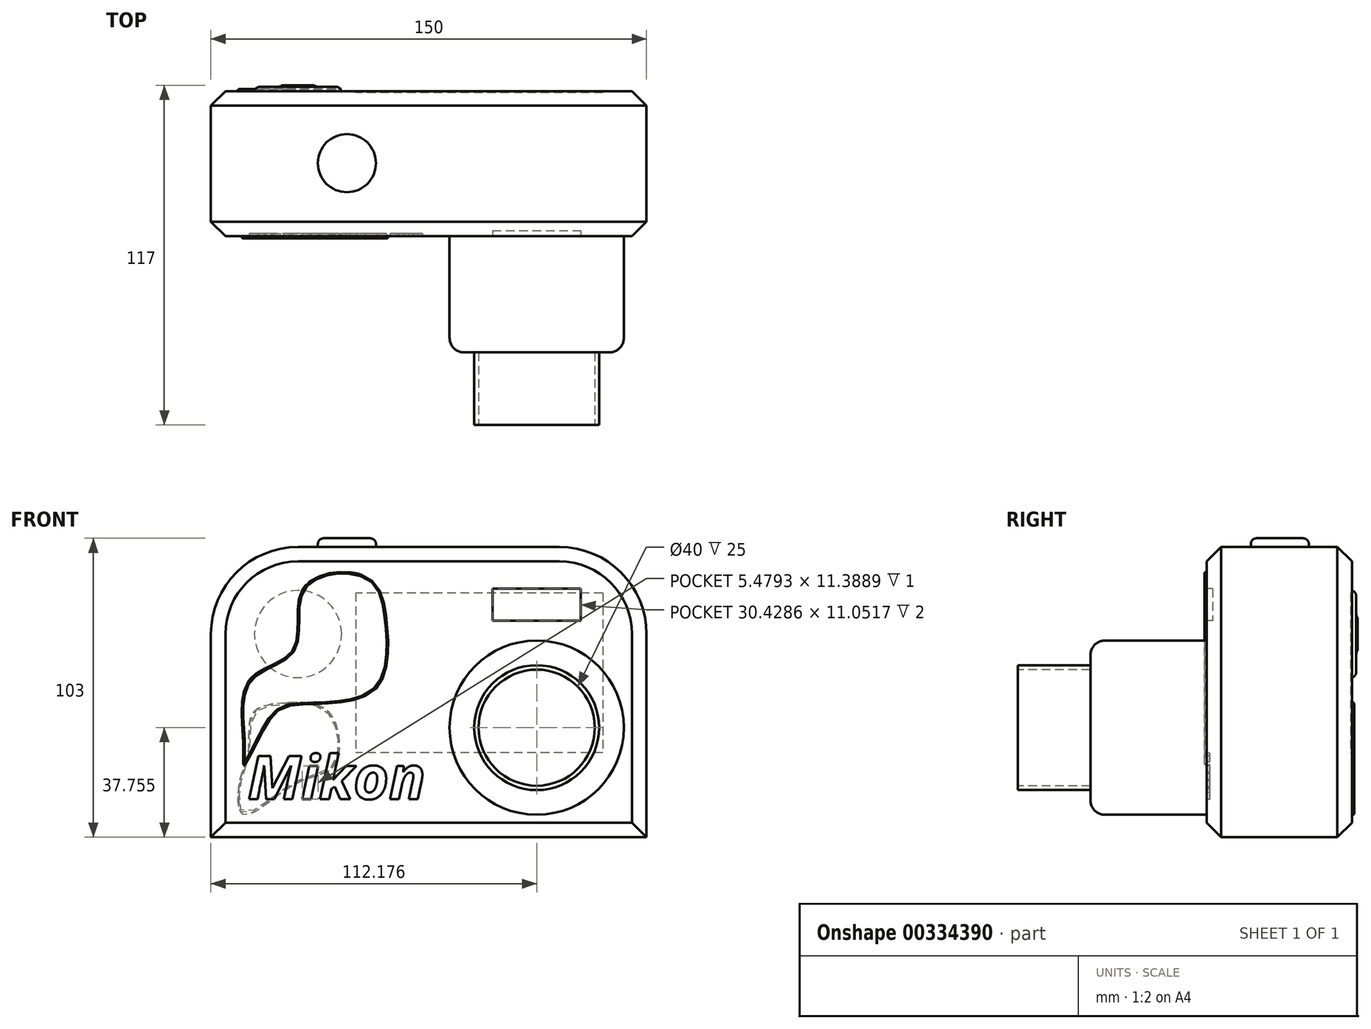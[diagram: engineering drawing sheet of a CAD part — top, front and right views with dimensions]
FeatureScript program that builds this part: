
annotation { "Feature Type Name" : "Feature", "Feature Type Description" : "" }
export const myFeature = defineFeature(function(context is Context, id is Id, definition is map)
    precondition{}
    {
        {
            var Q0;
            Q0=qCreatedBy(makeId("Top.planeOp"),FACE);
            var sketch = newSketch(context, id + "F0", { "sketchPlane" : qUnion([Q0])});
            skLineSegment(sketch, "E0.bottom", {"start": v(0, 0) * mm, "end": v(150, 0) * mm});
            skLineSegment(sketch, "E0.top", {"start": v(0, 50) * mm, "end": v(150, 50) * mm});
            skLineSegment(sketch, "E0.left", {"start": v(0, 0) * mm, "end": v(0, 50) * mm});
            skLineSegment(sketch, "E0.right", {"start": v(150, 0) * mm, "end": v(150, 50) * mm});
            skSolve(sketch);
        }
        {
            var Q0;
            Q0 = qSketchRegion(id + "F0", true);
            extrude(context, id + "F1", {"entities" : qUnion([Q0]), "depth" : 100 * mm});
        }
        {
            var Q0;
            Q0=makeQuery(id+"F1.opExtrude","SWEPT_FACE",FACE,{"disambiguationData":[OSD([sQuery(id+"F0.wireOp",EDGE,"E0.bottom")])]});
            var sketch = newSketch(context, id + "F2", { "sketchPlane" : qUnion([Q0])});
            skCircle(sketch, "E1", {"center": v(112.18, 37.75) * mm, "radius": 30 * mm});
            skSolve(sketch);
        }
        {
            var Q0;
            Q0 = qSketchRegion(id + "F2", true);
            extrude(context, id + "F3", {"entities" : qUnion([Q0]), "operationType" : NewBodyOperationType.ADD, "depth" : 40 * mm});
        }
        {
            var Q0;
            Q0=makeQuery(id+"F1.opExtrude","CAP_EDGE",EDGE,{"disambiguationData":[OSD([sQuery(id+"F0.wireOp",EDGE,"E0.right")])],"isStart":false});
            fillet(context, id + "F4", {"entities" : qUnion([Q0]), "radius" : 30 * mm, "tangentPropagation" : true, "allowEdgeOverflow" : false});
        }
        {
            var Q0;
            Q0=makeQuery(id+"F1.opExtrude","CAP_EDGE",EDGE,{"disambiguationData":[OSD([sQuery(id+"F0.wireOp",EDGE,"E0.left")])],"isStart":false});
            fillet(context, id + "F5", {"entities" : qUnion([Q0]), "radius" : 30 * mm, "tangentPropagation" : true, "allowEdgeOverflow" : false});
        }
        {
            var Q0;
            Q0=makeQuery(id+"F3.opExtrude","CAP_EDGE",EDGE,{"disambiguationData":[OSD([sQuery(id+"F2.wireOp",EDGE,"E1")])],"isStart":false});
            fillet(context, id + "F6", {"entities" : qUnion([Q0]), "radius" : 5 * mm, "tangentPropagation" : true, "allowEdgeOverflow" : false});
        }
        {
            var Q0;
            Q0=makeQuery(id+"F1.opExtrude","CAP_EDGE",EDGE,{"disambiguationData":[OSD([sQuery(id+"F0.wireOp",EDGE,"E0.bottom")])],"isStart":false});
            var Q1;
            Q1=makeQuery(id+"F1.opExtrude","CAP_EDGE",EDGE,{"disambiguationData":[OSD([sQuery(id+"F0.wireOp",EDGE,"E0.bottom")])],"isStart":true});
            var Q2;
            Q2=makeQuery(id+"F1.opExtrude","CAP_EDGE",EDGE,{"disambiguationData":[OSD([sQuery(id+"F0.wireOp",EDGE,"E0.top")])],"isStart":true});
            var Q3;
            Q3=makeQuery(id+"F1.opExtrude","SWEPT_EDGE",EDGE,{"disambiguationData":[OSD([sQuery(id+"F0.wireOp",EDGE,"E0.top"),sQuery(id+"F0.wireOp",EDGE,"E0.right")])]});
            chamfer(context, id + "F7", {"entities" : qUnion([Q0, Q1, Q2, Q3]), "width" : 5 * mm, "tangentPropagation" : true});
        }
        {
            var Q0;
            Q0=makeQuery(id+"F1.opExtrude","SWEPT_FACE",FACE,{"disambiguationData":[OSD([sQuery(id+"F0.wireOp",EDGE,"E0.bottom")])]});
            var sketch = newSketch(context, id + "F8", { "sketchPlane" : qUnion([Q0])});
            skText(sketch, "E2", { "text": "Mikon", "fontName": "OpenSans-BoldItalic.ttf"});
            const initialGuessF8  = {"E2": [0.01268, 0.01315, 1, 0, 0.01502]};
            skSetInitialGuess(sketch, initialGuessF8);
            skSolve(sketch);
        }
        {
            var Q0;
            Q0 = qSketchRegion(id + "F8", true);
            extrude(context, id + "F9", {"entities" : qUnion([Q0]), "operationType" : NewBodyOperationType.REMOVE, "oppositeDirection" : true, "depth" : 1 * mm});
        }
        {
            var Q0;
            Q0=makeQuery(id+"F1.opExtrude","CAP_FACE",FACE,{"disambiguationData":[OSD([sQuery(id+"F0.wireOp",EDGE,"E0.bottom"),sQuery(id+"F0.wireOp",EDGE,"E0.top"),sQuery(id+"F0.wireOp",EDGE,"E0.left"),sQuery(id+"F0.wireOp",EDGE,"E0.right")])],"isStart":false});
            var sketch = newSketch(context, id + "F10", { "sketchPlane" : qUnion([Q0])});
            skCircle(sketch, "E3", {"center": v(46.83, 25.2) * mm, "radius": 10 * mm});
            skSolve(sketch);
        }
        {
            var Q0;
            Q0 = qSketchRegion(id + "F10", true);
            extrude(context, id + "F11", {"entities" : qUnion([Q0]), "operationType" : NewBodyOperationType.ADD, "depth" : 3 * mm});
        }
        {
            var Q0;
            Q0=makeQuery(id+"F3.opExtrude","CAP_FACE",FACE,{"disambiguationData":[OSD([sQuery(id+"F2.wireOp",EDGE,"E1")])],"isStart":false});
            var sketch = newSketch(context, id + "F12", { "sketchPlane" : qUnion([Q0])});
            skCircle(sketch, "E4", {"center": v(112.18, 37.75) * mm, "radius": 21.5 * mm});
            skSolve(sketch);
        }
        {
            var Q0;
            Q0 = qSketchRegion(id + "F12", true);
            extrude(context, id + "F13", {"entities" : qUnion([Q0]), "operationType" : NewBodyOperationType.ADD, "depth" : 25 * mm});
        }
        {
            var Q0;
            Q0=makeQuery(id+"F13.opExtrude","CAP_FACE",FACE,{"disambiguationData":[OSD([sQuery(id+"F12.wireOp",EDGE,"E4")])],"isStart":false});
            var sketch = newSketch(context, id + "F14", { "sketchPlane" : qUnion([Q0])});
            skCircle(sketch, "E5", {"center": v(112.18, 37.75) * mm, "radius": 20 * mm});
            skSolve(sketch);
        }
        {
            var Q0;
            Q0 = qSketchRegion(id + "F14", true);
            extrude(context, id + "F15", {"entities" : qUnion([Q0]), "operationType" : NewBodyOperationType.REMOVE, "oppositeDirection" : true, "depth" : 25 * mm});
        }
        {
            var Q0;
            Q0=makeQuery(id+"F11.opExtrude","CAP_EDGE",EDGE,{"disambiguationData":[OSD([sQuery(id+"F10.wireOp",EDGE,"E3")])],"isStart":false});
            fillet(context, id + "F16", {"entities" : qUnion([Q0]), "radius" : 2 * mm, "tangentPropagation" : true, "allowEdgeOverflow" : false});
        }
        {
            var Q0;
            {var subQ0=sQuery(id+"F0.wireOp",EDGE,"E0.bottom");var subQ1=makeQuery(id+"F1.opExtrude","SWEPT_FACE",FACE,{"disambiguationData":[OSD([subQ0])]});var subQ2=subQ1;Q0=makeQuery(id+"F9.boolean.opBoolean","SPLIT",FACE,{"disambiguationData":[TD([makeQuery(id+"F3.opExtrude","SWEPT_FACE",FACE,{"disambiguationData":[OSD([sQuery(id+"F2.wireOp",EDGE,"E1")])]})])],"derivedFrom":subQ2});}
            var sketch = newSketch(context, id + "F17", { "sketchPlane" : qUnion([Q0])});
            skLineSegment(sketch, "E6.bottom", {"start": v(96.95, 85.64) * mm, "end": v(127.38, 85.64) * mm});
            skLineSegment(sketch, "E6.top", {"start": v(96.95, 74.59) * mm, "end": v(127.38, 74.59) * mm});
            skLineSegment(sketch, "E6.left", {"start": v(96.95, 85.64) * mm, "end": v(96.95, 74.59) * mm});
            skLineSegment(sketch, "E6.right", {"start": v(127.38, 85.64) * mm, "end": v(127.38, 74.59) * mm});
            skSolve(sketch);
        }
        {
            var Q0;
            Q0 = qSketchRegion(id + "F17", true);
            extrude(context, id + "F18", {"entities" : qUnion([Q0]), "operationType" : NewBodyOperationType.REMOVE, "oppositeDirection" : true, "depth" : 2 * mm});
        }
        {
            var Q0;
            Q0=makeQuery(id+"F1.opExtrude","SWEPT_FACE",FACE,{"disambiguationData":[OSD([sQuery(id+"F0.wireOp",EDGE,"E0.top")])]});
            var sketch = newSketch(context, id + "F19", { "sketchPlane" : qUnion([Q0])});
            skLineSegment(sketch, "E7.bottom", {"start": v(-134.92, 84.15) * mm, "end": v(-49.92, 84.15) * mm});
            skLineSegment(sketch, "E7.top", {"start": v(-134.92, 29.15) * mm, "end": v(-49.92, 29.15) * mm});
            skLineSegment(sketch, "E7.left", {"start": v(-134.92, 84.15) * mm, "end": v(-134.92, 29.15) * mm});
            skLineSegment(sketch, "E7.right", {"start": v(-49.92, 84.15) * mm, "end": v(-49.92, 29.15) * mm});
            skSolve(sketch);
        }
        {
            var Q0;
            Q0 = qSketchRegion(id + "F19", true);
            extrude(context, id + "F20", {"entities" : qUnion([Q0]), "operationType" : NewBodyOperationType.REMOVE, "oppositeDirection" : true, "depth" : 0.5 * mm});
        }
        {
            var Q0;
            {var subQ0=sQuery(id+"F0.wireOp",EDGE,"E0.bottom");var subQ1=makeQuery(id+"F1.opExtrude","SWEPT_FACE",FACE,{"disambiguationData":[OSD([subQ0])]});var subQ2=subQ1;Q0=makeQuery(id+"F9.boolean.opBoolean","SPLIT",FACE,{"disambiguationData":[TD([makeQuery(id+"F3.opExtrude","SWEPT_FACE",FACE,{"disambiguationData":[OSD([sQuery(id+"F2.wireOp",EDGE,"E1")])]})])],"derivedFrom":subQ2});}
            var sketch = newSketch(context, id + "F21", { "sketchPlane" : qUnion([Q0])});
            skFitSpline(sketch, "E8", {"points": [v(11.15, 31.94) * mm, v(13.36, 54.3) * mm, v(28.42, 64.71) * mm, v(31.96, 85.97) * mm, v(53.44, 89.73) * mm, v(60.53, 74.01) * mm, v(56.1, 50.54) * mm, v(30.2, 45.67) * mm, v(20.23, 40.57) * mm, v(11.6, 24.85) * mm, v(11.15, 31.94) * mm]});
            skSolve(sketch);
        }
        {
            var Q0;
            Q0 = qSketchRegion(id + "F21", true);
            extrude(context, id + "F22", {"entities" : qUnion([Q0]), "operationType" : NewBodyOperationType.ADD, "depth" : 0.75 * mm});
        }
        {
            var Q0;
            Q0=makeQuery(id+"F22.opExtrude","CAP_EDGE",EDGE,{"disambiguationData":[OSD([sQuery(id+"F21.wireOp",EDGE,"E8")])],"isStart":false});
            fillet(context, id + "F23", {"entities" : qUnion([Q0]), "radius" : 0.5 * mm, "tangentPropagation" : true, "allowEdgeOverflow" : false});
        }
        {
            var Q0;
            Q0=makeQuery(id+"F1.opExtrude","SWEPT_FACE",FACE,{"disambiguationData":[OSD([sQuery(id+"F0.wireOp",EDGE,"E0.top")])]});
            var sketch = newSketch(context, id + "F24", { "sketchPlane" : qUnion([Q0])});
            skFitSpline(sketch, "E9", {"points": [v(-25.98, 46.33) * mm, v(-40.82, 43) * mm, v(-42.81, 25.07) * mm, v(-29.53, 18.65) * mm, v(-11.15, 7.8) * mm, v(-10.04, 19.76) * mm, v(-12.92, 29.94) * mm, v(-14.47, 42.79) * mm, v(-25.98, 46.33) * mm]});
            skSolve(sketch);
        }
        {
            var Q0;
            Q0 = qSketchRegion(id + "F24", true);
            extrude(context, id + "F25", {"entities" : qUnion([Q0]), "operationType" : NewBodyOperationType.ADD, "depth" : 0.75 * mm});
        }
        {
            var Q0;
            Q0=makeQuery(id+"F25.opExtrude","CAP_EDGE",EDGE,{"disambiguationData":[OSD([sQuery(id+"F24.wireOp",EDGE,"E9")])],"isStart":false});
            fillet(context, id + "F26", {"entities" : qUnion([Q0]), "radius" : 0.5 * mm, "tangentPropagation" : true, "allowEdgeOverflow" : false});
        }
        {
            var Q0;
            Q0=makeQuery(id+"F1.opExtrude","SWEPT_FACE",FACE,{"disambiguationData":[OSD([sQuery(id+"F0.wireOp",EDGE,"E0.top")])]});
            var sketch = newSketch(context, id + "F27", { "sketchPlane" : qUnion([Q0])});
            skCircle(sketch, "E10", {"center": v(-30, 70) * mm, "radius": 15 * mm});
            skCircle(sketch, "E11", {"center": v(-30, 70) * mm, "radius": 6 * mm});
            skSolve(sketch);
        }
        {
            var Q0;
            Q0=makeQuery(id+"F27.imprint","IMPRINT",FACE,{"disambiguationData":[TD([[makeQuery(id+"F27.imprint","IMPRINT",EDGE,{"derivedFrom":sQuery(id+"F27.wireOp",EDGE,"E11")}),1.0]])]});
            var Q1;
            Q1=sQuery(id+"F27.wireOp",EDGE,"E11");
            extrude(context, id + "F28", {"entities" : qUnion([Q0]), "operationType" : NewBodyOperationType.ADD, "surfaceEntities" : qUnion([Q1]), "depth" : 2 * mm});
        }
        {
            var Q0;
            Q0 = qSketchRegion(id + "F27", true);
            extrude(context, id + "F29", {"entities" : qUnion([Q0]), "operationType" : NewBodyOperationType.ADD, "depth" : 1.5 * mm});
        }
        {
            var Q0;
            Q0=makeQuery(id+"F28.opExtrude","CAP_EDGE",EDGE,{"disambiguationData":[OSD([sQuery(id+"F27.wireOp",EDGE,"E11")])],"isStart":false});
            fillet(context, id + "F30", {"entities" : qUnion([Q0]), "radius" : 1 * mm, "tangentPropagation" : true, "allowEdgeOverflow" : false});
        }
        {
            var Q0;
            {var subQ0=sQuery(id+"F27.wireOp",EDGE,"E11");Q0=makeQuery(id+"F30.opFillet","BLEND_EDGE",EDGE,{"blendedFrom":[makeQuery(id+"F28.opExtrude","CAP_EDGE",EDGE,{"disambiguationData":[OSD([subQ0])],"isStart":false}),makeQuery(id+"F29.opExtrude","CAP_FACE",FACE,{"disambiguationData":[OSD([sQuery(id+"F27.wireOp",EDGE,"E10"),subQ0])],"isStart":false})],"blendedInto":[makeQuery(id+"F29.opExtrude","CAP_FACE",FACE,{"disambiguationData":[OSD([sQuery(id+"F27.wireOp",EDGE,"E10"),subQ0])],"isStart":false})]});}
            fillet(context, id + "F31", {"entities" : qUnion([Q0]), "radius" : 3 * mm, "tangentPropagation" : true, "allowEdgeOverflow" : false});
        }
        {
            var Q0;
            Q0=makeQuery(id+"F29.opExtrude","CAP_EDGE",EDGE,{"disambiguationData":[OSD([sQuery(id+"F27.wireOp",EDGE,"E10")])],"isStart":false});
            fillet(context, id + "F32", {"entities" : qUnion([Q0]), "radius" : 2 * mm, "tangentPropagation" : true, "allowEdgeOverflow" : false});
        }
    });
